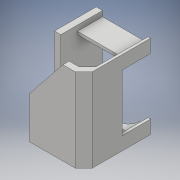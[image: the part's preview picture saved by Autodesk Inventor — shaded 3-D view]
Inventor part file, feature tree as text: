
AUTODESK INVENTOR PART (.ipt)
format: ipt  version: 2018 (Build 220112000, 112)  size: 231,424 bytes
history: native  units: in
note: dims shown in document units (in); Inventor stores cm internally (conversion verified against a paired STEP export)
features: extrude x10, sketch x10
ambient origin geometry x8: Origin, YZ Plane, XZ Plane, XY Plane, X Axis, Y Axis, Z Axis, Center Point
bodies: Solid1 (feature_tree)
feature tree (20):
  extrude  "Extrusion1"  Depth=2.5591in
  extrude  "Extrusion2"  Depth=0.4921in
  sketch  "Sketch3"  dims[d5=0.2953in d6=0.1181in]
  extrude  "Extrusion4"  Depth=0.1181in
  extrude  "Extrusion5"  Depth=0.2953in
  sketch  "Sketch7"  dims[d11=3.937in d12=0.0in d13=3.6811in]
  extrude  "Extrusion6"  Depth=0.3937in
  extrude  "Extrusion7"  Depth=3.6811in
  extrude  "Extrusion8"  Depth=1.1811in TaperAngle=0.0deg
  extrude  "Extrusion9"  Depth=0.6299in
  extrude  "Extrusion10"  Depth=2.6772in
  extrude  "Extrusion11"  Depth=0.5906in
  sketch  "Sketch1"  dims[d0=3.1496in d1=2.5591in]
  sketch  "Sketch2"  dims[d3=0.5512in d4=0.4921in]
  sketch  "Sketch4"  dims[d7=0.689in d8=0.2953in]
  sketch  "Sketch5"  dims[d9=0.3937in d10=0.3937in]
  sketch  "Sketch8"  dims[d14=2.1457in d15=1.1811in d16=0.0in]
  sketch  "Sketch9"  dims[d22=1.3386in d23=0.6299in]
  sketch  "Sketch10"  dims[d24=0.6299in d25=2.6772in]
  sketch  "Sketch11"  dims[d26=1.1811in d27=0.0in d28=0.5906in d29=0.0591in d30=0.0in d31=0.0591in d32=1.1811in d33=0.0in d39=1.5748in d40=0.9843in d41=1.9685in d43=0.2953in d44=0.2953in d45=0.1181in d46=1.1811in d47=0.0in d48=0.3937in d49=0.3937in d50=0.3937in d51=0.3937in d52=3.937in d53=0.0in d54=1.1811in d55=0.0in d56=0.5906in d57=0.7874in d58=1.1811in d59=0.0in d60=1.1811in d61=0.0in d62=0.1378in d63=1.1811in d64=0.3937in d65=1.1811in d66=0.0in]
